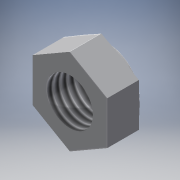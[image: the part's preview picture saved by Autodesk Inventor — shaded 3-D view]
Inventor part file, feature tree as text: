
AUTODESK INVENTOR PART (.ipt)
format: ipt  version: 2016 (Build 200138000, 138)  size: 148,992 bytes
history: native  units: mm
features: extrude x2, sketch x2, fillet x1, thread x1
ambient origin geometry x8: Origin, YZ Plane, XZ Plane, XY Plane, X Axis, Y Axis, Z Axis, Center Point
bodies: Solid1 (feature_tree)
feature tree (6):
  extrude  "Extrusion1"  Depth=13.0mm
  extrude  "Extrusion2"  Depth=1.5mm
  fillet  "Fillet1"  Radius=1.5mm
  thread  "Thread2"  [1 undecoded]
  sketch  "Sketch1"  dims[d0=8.0mm d1=13.0mm]
  sketch  "Sketch2"  dims[d2=5.5mm d3=0.0mm d6=2.0mm d7=1.5mm d8=0.0mm d9=1.5mm d10=10.0mm d11=0.0mm]
note: 1 required parameter value undecoded (feature->parameter linkage not recoverable at this tier; creation-order binding heuristic only, values carry confidence <= 0.55)
